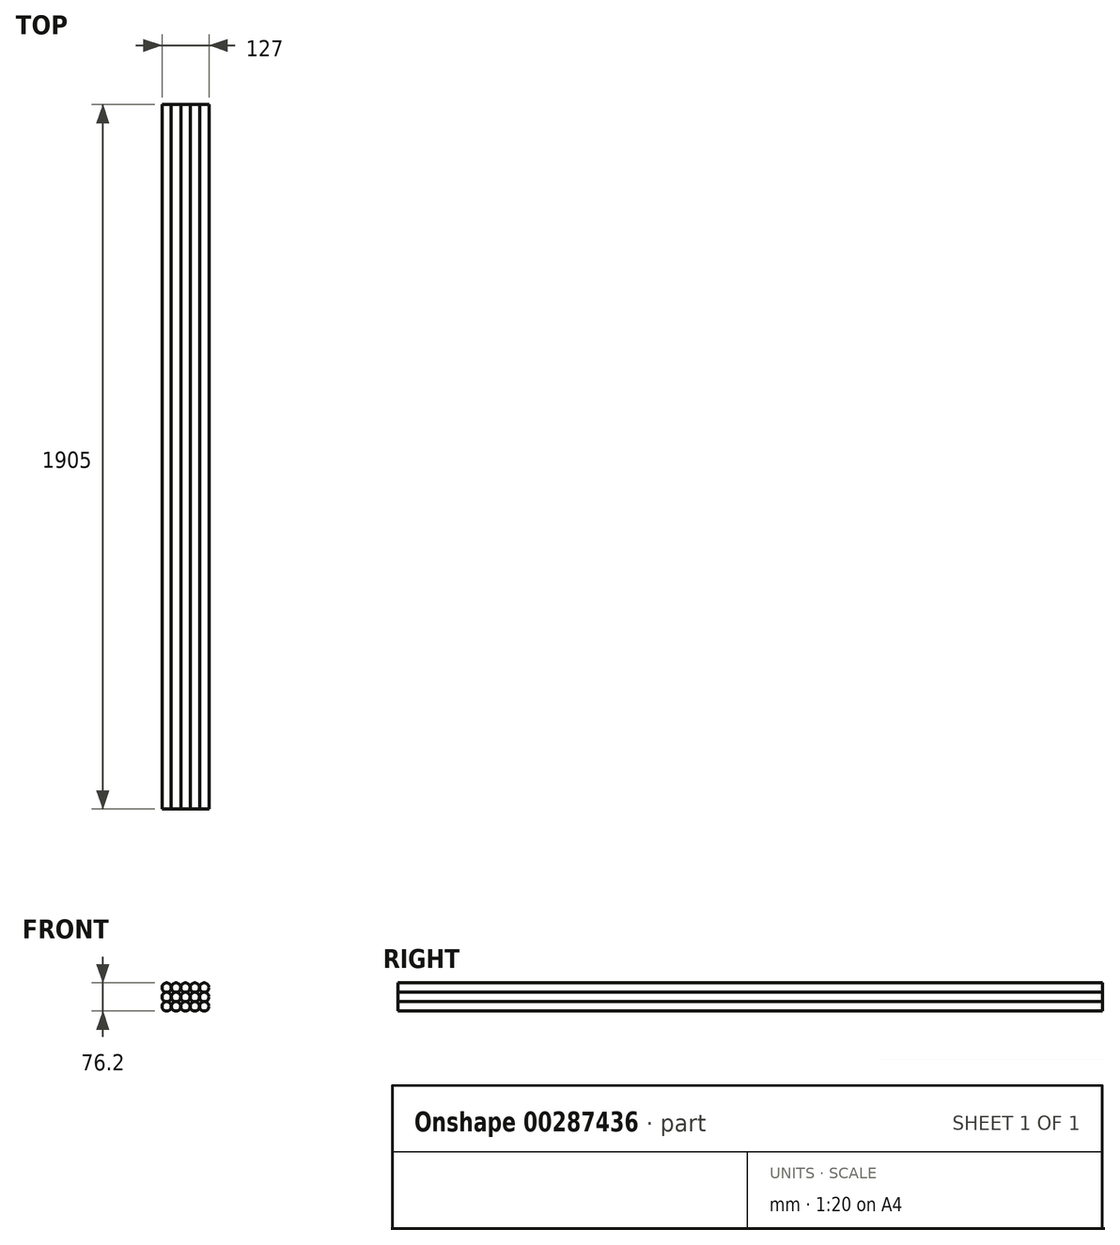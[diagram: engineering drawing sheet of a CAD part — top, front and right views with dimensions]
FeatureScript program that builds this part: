
annotation { "Feature Type Name" : "Feature", "Feature Type Description" : "" }
export const myFeature = defineFeature(function(context is Context, id is Id, definition is map)
    precondition{}
    {
        {
            var Q0;
            Q0=qCreatedBy(makeId("Front.planeOp"),FACE);
            var sketch = newSketch(context, id + "F0", { "sketchPlane" : qUnion([Q0])});
            skCircle(sketch, "E0", {"center": v(0, 0) * mm, "radius": 12.7 * mm});
            skCircle(sketch, "E1", {"center": v(25.4, 0) * mm, "radius": 12.7 * mm});
            skCircle(sketch, "E2", {"center": v(50.8, 0) * mm, "radius": 12.7 * mm});
            skCircle(sketch, "E3", {"center": v(76.2, 0) * mm, "radius": 12.7 * mm});
            skCircle(sketch, "E4", {"center": v(101.6, -25.4) * mm, "radius": 12.7 * mm});
            skCircle(sketch, "E5", {"center": v(0, -25.4) * mm, "radius": 12.7 * mm});
            skCircle(sketch, "E6", {"center": v(0, -50.8) * mm, "radius": 12.7 * mm});
            skCircle(sketch, "E7", {"center": v(25.4, -25.4) * mm, "radius": 12.7 * mm});
            skCircle(sketch, "E8", {"center": v(76.2, -25.4) * mm, "radius": 12.7 * mm});
            skCircle(sketch, "E9", {"center": v(101.6, 0) * mm, "radius": 12.7 * mm});
            skCircle(sketch, "E10", {"center": v(25.4, -50.8) * mm, "radius": 12.7 * mm});
            skCircle(sketch, "E11", {"center": v(50.8, -25.4) * mm, "radius": 12.7 * mm});
            skCircle(sketch, "E12", {"center": v(50.8, -50.8) * mm, "radius": 12.7 * mm});
            skCircle(sketch, "E13", {"center": v(76.2, -50.8) * mm, "radius": 12.7 * mm});
            skCircle(sketch, "E14", {"center": v(101.6, -50.8) * mm, "radius": 12.7 * mm});
            skSolve(sketch);
        }
        {
            var Q0;
            {var subQ0=sQuery(id+"F0.wireOp",EDGE,"E0");var subQ1=makeQuery(id+"F0.imprint","INTERSECT",VERTEX,{"derivedFrom":[subQ0,sQuery(id+"F0.wireOp",EDGE,"E1")]});Q0=makeQuery(id+"F0.imprint","IMPRINT",FACE,{"disambiguationData":[TD([[makeQuery(id+"F0.imprint","IMPRINT",EDGE,{"disambiguationData":[TD([[subQ1,-1.0]])],"derivedFrom":subQ0}),1.0]])]});}
            var Q1;
            {var subQ0=sQuery(id+"F0.wireOp",EDGE,"E1");var subQ1=makeQuery(id+"F0.imprint","INTERSECT",VERTEX,{"derivedFrom":[sQuery(id+"F0.wireOp",EDGE,"E0"),subQ0]});Q1=makeQuery(id+"F0.imprint","IMPRINT",FACE,{"disambiguationData":[TD([[makeQuery(id+"F0.imprint","IMPRINT",EDGE,{"disambiguationData":[TD([[subQ1,1.0]])],"derivedFrom":subQ0}),1.0]])]});}
            var Q2;
            {var subQ0=sQuery(id+"F0.wireOp",EDGE,"E2");var subQ1=makeQuery(id+"F0.imprint","INTERSECT",VERTEX,{"derivedFrom":[sQuery(id+"F0.wireOp",EDGE,"E1"),subQ0]});Q2=makeQuery(id+"F0.imprint","IMPRINT",FACE,{"disambiguationData":[TD([[makeQuery(id+"F0.imprint","IMPRINT",EDGE,{"disambiguationData":[TD([[subQ1,1.0]])],"derivedFrom":subQ0}),1.0]])]});}
            var Q3;
            {var subQ0=sQuery(id+"F0.wireOp",EDGE,"E3");var subQ1=makeQuery(id+"F0.imprint","INTERSECT",VERTEX,{"derivedFrom":[sQuery(id+"F0.wireOp",EDGE,"E2"),subQ0]});Q3=makeQuery(id+"F0.imprint","IMPRINT",FACE,{"disambiguationData":[TD([[makeQuery(id+"F0.imprint","IMPRINT",EDGE,{"disambiguationData":[TD([[subQ1,-1.0]])],"derivedFrom":subQ0}),1.0]])]});}
            var Q4;
            {var subQ0=sQuery(id+"F0.wireOp",EDGE,"E9");var subQ1=makeQuery(id+"F0.imprint","INTERSECT",VERTEX,{"derivedFrom":[sQuery(id+"F0.wireOp",EDGE,"E3"),subQ0]});Q4=makeQuery(id+"F0.imprint","IMPRINT",FACE,{"disambiguationData":[TD([[makeQuery(id+"F0.imprint","IMPRINT",EDGE,{"disambiguationData":[TD([[subQ1,-1.0]])],"derivedFrom":subQ0}),1.0]])]});}
            var Q5;
            {var subQ0=sQuery(id+"F0.wireOp",EDGE,"E4");var subQ1=makeQuery(id+"F0.imprint","INTERSECT",VERTEX,{"derivedFrom":[subQ0,sQuery(id+"F0.wireOp",EDGE,"E9")]});Q5=makeQuery(id+"F0.imprint","IMPRINT",FACE,{"disambiguationData":[TD([[makeQuery(id+"F0.imprint","IMPRINT",EDGE,{"disambiguationData":[TD([[subQ1,1.0]])],"derivedFrom":subQ0}),1.0]])]});}
            var Q6;
            {var subQ0=sQuery(id+"F0.wireOp",EDGE,"E8");var subQ1=makeQuery(id+"F0.imprint","INTERSECT",VERTEX,{"derivedFrom":[sQuery(id+"F0.wireOp",EDGE,"E4"),subQ0]});Q6=makeQuery(id+"F0.imprint","IMPRINT",FACE,{"disambiguationData":[TD([[makeQuery(id+"F0.imprint","IMPRINT",EDGE,{"disambiguationData":[TD([[subQ1,1.0]])],"derivedFrom":subQ0}),1.0]])]});}
            var Q7;
            {var subQ0=sQuery(id+"F0.wireOp",EDGE,"E11");var subQ1=makeQuery(id+"F0.imprint","INTERSECT",VERTEX,{"derivedFrom":[sQuery(id+"F0.wireOp",EDGE,"E2"),subQ0]});Q7=makeQuery(id+"F0.imprint","IMPRINT",FACE,{"disambiguationData":[TD([[makeQuery(id+"F0.imprint","IMPRINT",EDGE,{"disambiguationData":[TD([[subQ1,-1.0]])],"derivedFrom":subQ0}),1.0]])]});}
            var Q8;
            {var subQ0=sQuery(id+"F0.wireOp",EDGE,"E7");var subQ1=makeQuery(id+"F0.imprint","INTERSECT",VERTEX,{"derivedFrom":[sQuery(id+"F0.wireOp",EDGE,"E1"),subQ0]});Q8=makeQuery(id+"F0.imprint","IMPRINT",FACE,{"disambiguationData":[TD([[makeQuery(id+"F0.imprint","IMPRINT",EDGE,{"disambiguationData":[TD([[subQ1,1.0]])],"derivedFrom":subQ0}),1.0]])]});}
            var Q9;
            {var subQ0=sQuery(id+"F0.wireOp",EDGE,"E5");var subQ1=makeQuery(id+"F0.imprint","INTERSECT",VERTEX,{"derivedFrom":[sQuery(id+"F0.wireOp",EDGE,"E0"),subQ0]});Q9=makeQuery(id+"F0.imprint","IMPRINT",FACE,{"disambiguationData":[TD([[makeQuery(id+"F0.imprint","IMPRINT",EDGE,{"disambiguationData":[TD([[subQ1,1.0]])],"derivedFrom":subQ0}),1.0]])]});}
            var Q10;
            {var subQ0=sQuery(id+"F0.wireOp",EDGE,"E6");var subQ1=makeQuery(id+"F0.imprint","INTERSECT",VERTEX,{"derivedFrom":[sQuery(id+"F0.wireOp",EDGE,"E5"),subQ0]});Q10=makeQuery(id+"F0.imprint","IMPRINT",FACE,{"disambiguationData":[TD([[makeQuery(id+"F0.imprint","IMPRINT",EDGE,{"disambiguationData":[TD([[subQ1,1.0]])],"derivedFrom":subQ0}),1.0]])]});}
            var Q11;
            {var subQ0=sQuery(id+"F0.wireOp",EDGE,"E10");var subQ1=makeQuery(id+"F0.imprint","INTERSECT",VERTEX,{"derivedFrom":[subQ0,sQuery(id+"F0.wireOp",EDGE,"E12")]});Q11=makeQuery(id+"F0.imprint","IMPRINT",FACE,{"disambiguationData":[TD([[makeQuery(id+"F0.imprint","IMPRINT",EDGE,{"disambiguationData":[TD([[subQ1,-1.0]])],"derivedFrom":subQ0}),1.0]])]});}
            var Q12;
            {var subQ0=sQuery(id+"F0.wireOp",EDGE,"E12");var subQ1=makeQuery(id+"F0.imprint","INTERSECT",VERTEX,{"derivedFrom":[sQuery(id+"F0.wireOp",EDGE,"E10"),subQ0]});Q12=makeQuery(id+"F0.imprint","IMPRINT",FACE,{"disambiguationData":[TD([[makeQuery(id+"F0.imprint","IMPRINT",EDGE,{"disambiguationData":[TD([[subQ1,1.0]])],"derivedFrom":subQ0}),1.0]])]});}
            var Q13;
            {var subQ0=sQuery(id+"F0.wireOp",EDGE,"E13");var subQ1=makeQuery(id+"F0.imprint","INTERSECT",VERTEX,{"derivedFrom":[sQuery(id+"F0.wireOp",EDGE,"E12"),subQ0]});Q13=makeQuery(id+"F0.imprint","IMPRINT",FACE,{"disambiguationData":[TD([[makeQuery(id+"F0.imprint","IMPRINT",EDGE,{"disambiguationData":[TD([[subQ1,1.0]])],"derivedFrom":subQ0}),1.0]])]});}
            var Q14;
            {var subQ0=sQuery(id+"F0.wireOp",EDGE,"E14");var subQ1=makeQuery(id+"F0.imprint","INTERSECT",VERTEX,{"derivedFrom":[sQuery(id+"F0.wireOp",EDGE,"E4"),subQ0]});Q14=makeQuery(id+"F0.imprint","IMPRINT",FACE,{"disambiguationData":[TD([[makeQuery(id+"F0.imprint","IMPRINT",EDGE,{"disambiguationData":[TD([[subQ1,-1.0]])],"derivedFrom":subQ0}),1.0]])]});}
            extrude(context, id + "F1", {"entities" : qUnion([Q0, Q1, Q2, Q3, Q4, Q5, Q6, Q7, Q8, Q9, Q10, Q11, Q12, Q13, Q14]), "depth" : 1905 * mm});
        }
    });
